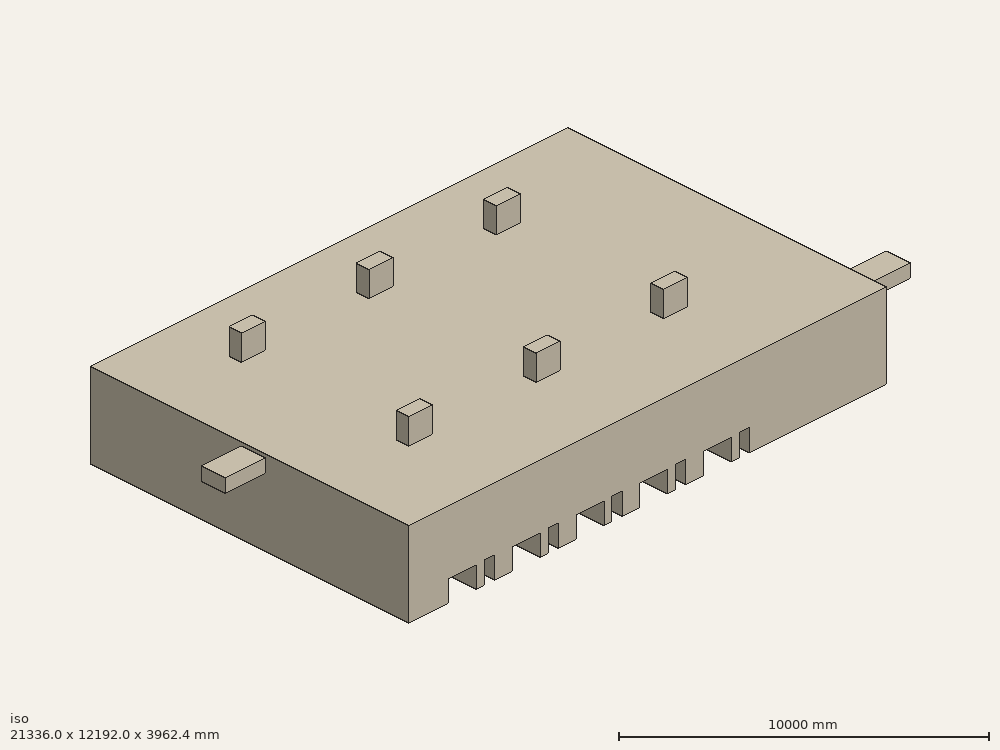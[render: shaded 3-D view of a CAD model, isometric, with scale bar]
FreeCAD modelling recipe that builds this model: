
FCSTD DOCUMENT  (FreeCAD 0.18R14555 (Git shallow))
Label: flow_domain
License: All rights reserved
LicenseURL: http://en.wikipedia.org/wiki/All_rights_reserved
objects: Part::Box×20, Part::MultiFuse×12, Part::Mirroring×1, Part::Cut×1
note: 34 computed .brp shape members not serialized (recipe doc carries the construction recipe); baked Part::Feature solids carry a one-line shape summary decoded from their .brp

FEATURE [Part::Box] Box001  label="Bed 1"
  AttacherType = Attacher::AttachEngine3D
  Height = 762
  Length = 1066.8
  Width = 1981.2
FEATURE [Part::Box] Box002  label="Table 1"
  AttacherType = Attacher::AttachEngine3D
  Height = 798.576
  Length = 396.24
  Placement = pos=(1371.6,0,0) rot=(0,0,1;0rad)
  Width = 396.24
FEATURE [Part::MultiFuse] Fusion  label="Set 1"
  Shapes = -> [Box002,Box001]
FEATURE [Part::Box] Box003  label="Bed 002"
  AttacherType = Attacher::AttachEngine3D
  Height = 762
  Length = 1066.8
  Width = 1981.2
FEATURE [Part::Box] Box004  label="Table 002"
  AttacherType = Attacher::AttachEngine3D
  Height = 798.576
  Length = 396.24
  Placement = pos=(1371.6,0,0) rot=(0,0,1;0rad)
  Width = 396.24
FEATURE [Part::MultiFuse] Fusion001  label="Set 2"
  Placement = pos=(2438.4,0,0) rot=(0,0,1;0rad)
  Shapes = -> [Box004,Box003]
FEATURE [Part::Box] Box005  label="Table 003"
  AttacherType = Attacher::AttachEngine3D
  Height = 798.576
  Length = 396.24
  Placement = pos=(1371.6,0,0) rot=(0,0,1;0rad)
  Width = 396.24
FEATURE [Part::Box] Box006  label="Bed 003"
  AttacherType = Attacher::AttachEngine3D
  Height = 762
  Length = 1066.8
  Width = 1981.2
FEATURE [Part::MultiFuse] Fusion002  label="Set 3"
  Placement = pos=(4876.8,0,0) rot=(0,0,1;0rad)
  Shapes = -> [Box005,Box006]
FEATURE [Part::Box] Box007  label="Bed 004"
  AttacherType = Attacher::AttachEngine3D
  Height = 762
  Length = 1066.8
  Width = 1981.2
FEATURE [Part::Box] Box008  label="Table 004"
  AttacherType = Attacher::AttachEngine3D
  Height = 798.576
  Length = 396.24
  Placement = pos=(1371.6,0,0) rot=(0,0,1;0rad)
  Width = 396.24
FEATURE [Part::MultiFuse] Fusion003  label="Set 4"
  Placement = pos=(7315.2,0,0) rot=(0,0,1;0rad)
  Shapes = -> [Box008,Box007]
FEATURE [Part::Box] Box009  label="Table 005"
  AttacherType = Attacher::AttachEngine3D
  Height = 798.576
  Length = 396.24
  Placement = pos=(1371.6,0,0) rot=(0,0,1;0rad)
  Width = 396.24
FEATURE [Part::Box] Box010  label="Bed 005"
  AttacherType = Attacher::AttachEngine3D
  Height = 762
  Length = 1066.8
  Width = 1981.2
FEATURE [Part::MultiFuse] Fusion004  label="Set 5"
  Placement = pos=(9753.6,0,0) rot=(0,0,1;0rad)
  Shapes = -> [Box009,Box010]
FEATURE [Part::MultiFuse] Fusion005  label="right beds"
  Shapes = -> [Fusion001,Fusion002,Fusion003,Fusion004,Fusion]
FEATURE [Part::Mirroring] Part__Mirroring  label="left beds"
  Base = (0,6096,0)
  Normal = (0,1,0)
  Source = -> Fusion005
FEATURE [Part::Box] Box011  label="Nurse Station"
  AttacherType = Attacher::AttachEngine3D
  Height = 1219.2
  Length = 3048
  Placement = pos=(15240,7620,0) rot=(0,0,1;0rad)
  Width = 4572
FEATURE [Part::Box] Box012  label="main inlet"
  AttacherType = Attacher::AttachEngine3D
  Height = 487.68
  Length = 2438.4
  Placement = pos=(17373.6,609.6,2438.4) rot=(0,0,1;0rad)
  Width = 914.4
FEATURE [Part::Box] Box013  label="main outlet"
  AttacherType = Attacher::AttachEngine3D
  Height = 487.68
  Length = 2438.4
  Placement = pos=(-1524,5486.4,2438.4) rot=(0,0,1;0rad)
  Width = 914.4
FEATURE [Part::Box] Box014  label="branch"
  AttacherType = Attacher::AttachEngine3D
  Height = 1219.2
  Length = 914.4
  Placement = pos=(12801.6,9448.8,2743.2) rot=(0,0,1;0rad)
  Width = 487.68
FEATURE [Part::Box] Box015  label="branch001"
  AttacherType = Attacher::AttachEngine3D
  Height = 1219.2
  Length = 914.4
  Placement = pos=(12801.6,3048,2743.2) rot=(0,0,1;0rad)
  Width = 487.68
FEATURE [Part::Box] Box016  label="branch002"
  AttacherType = Attacher::AttachEngine3D
  Height = 1219.2
  Length = 914.4
  Placement = pos=(7924.8,3048,2743.2) rot=(0,0,1;0rad)
  Width = 487.68
FEATURE [Part::Box] Box017  label="branch003"
  AttacherType = Attacher::AttachEngine3D
  Height = 1219.2
  Length = 914.4
  Placement = pos=(7924.8,9448.8,2743.2) rot=(0,0,1;0rad)
  Width = 487.68
FEATURE [Part::Box] Box018  label="branch004"
  AttacherType = Attacher::AttachEngine3D
  Height = 1219.2
  Length = 914.4
  Placement = pos=(3048,3048,2743.2) rot=(0,0,1;0rad)
  Width = 487.68
FEATURE [Part::Box] Box019  label="branch005"
  AttacherType = Attacher::AttachEngine3D
  Height = 1219.2
  Length = 914.4
  Placement = pos=(3048,9448.8,2743.2) rot=(0,0,1;0rad)
  Width = 487.68
FEATURE [Part::MultiFuse] Fusion006  label="all beds"
  Placement = pos=(1524,0,0) rot=(0,0,1;0rad)
  Shapes = -> [Part__Mirroring,Fusion005]
FEATURE [Part::MultiFuse] Fusion007  label="branch ducts"
  Shapes = -> [Box019,Box016,Box018,Box017,Box015,Box014]
FEATURE [Part::Box] Box  label="Room"
  AttacherType = Attacher::AttachEngine3D
  Height = 3048
  Length = 18288
  Width = 12192
FEATURE [Part::MultiFuse] Fusion008  label="main ducts"
  Shapes = -> [Box012,Box013]
FEATURE [Part::MultiFuse] Fusion009  label="all ducts"
  Shapes = -> [Fusion008,Fusion007]
FEATURE [Part::MultiFuse] Fusion010  label="Overall Room"
  Shapes = -> [Box,Fusion009]
FEATURE [Part::MultiFuse] Fusion011  label="All_Surfaces"
  Shapes = -> [Fusion006,Box011]
FEATURE [Part::Cut] Cut  label="Flow_field"
  Base = -> Fusion010
  Tool = -> Fusion011
